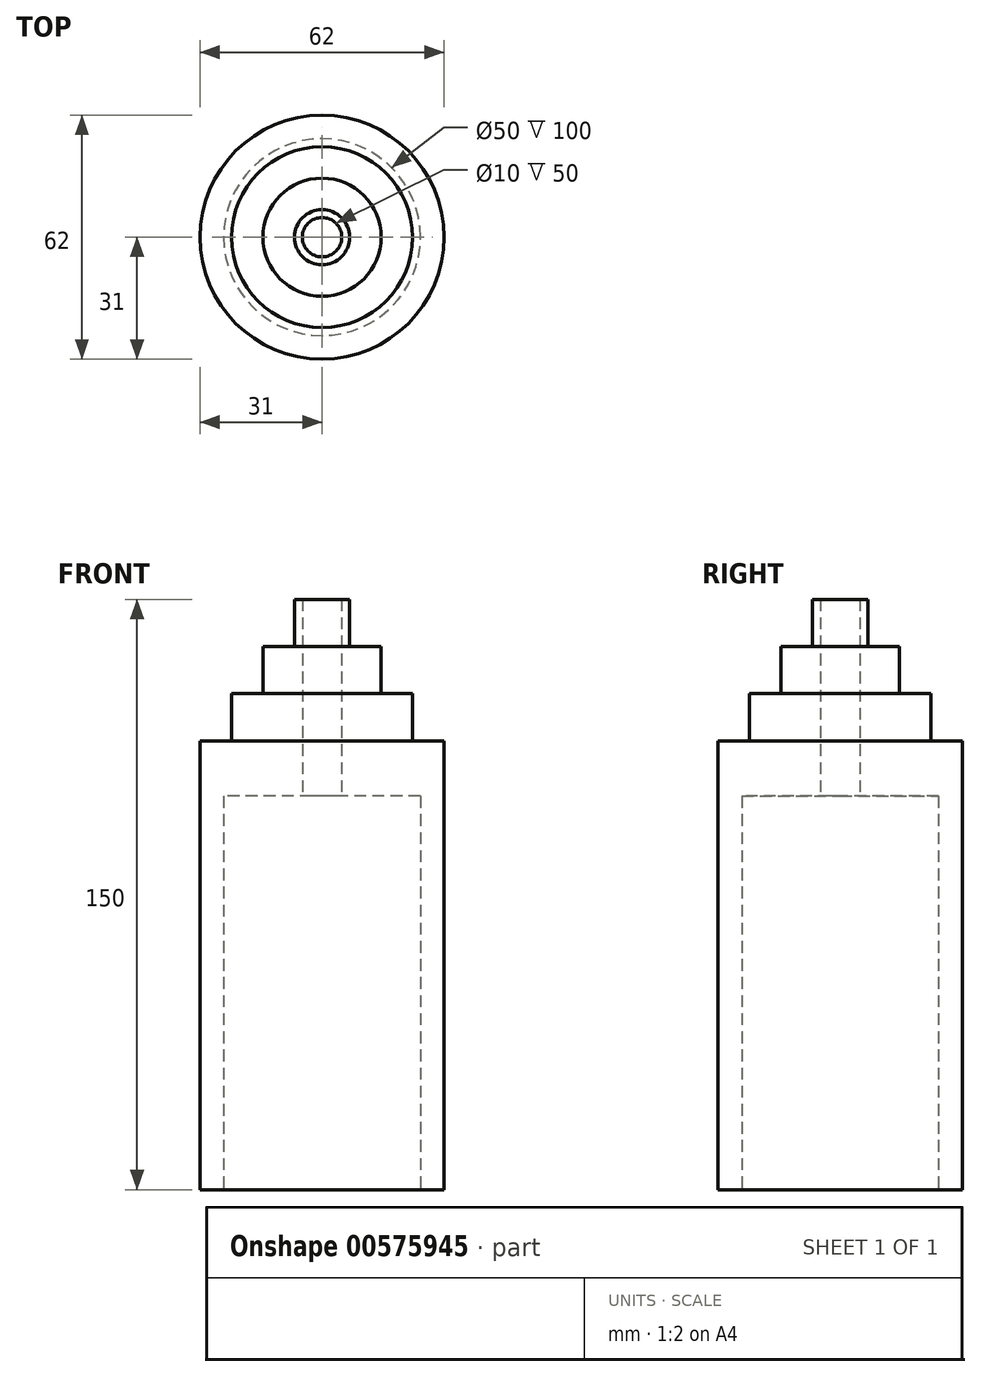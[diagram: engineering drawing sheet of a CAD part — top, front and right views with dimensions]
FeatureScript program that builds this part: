
annotation { "Feature Type Name" : "Feature", "Feature Type Description" : "" }
export const myFeature = defineFeature(function(context is Context, id is Id, definition is map)
    precondition{}
    {
        {
            var Q0;
            Q0=qCreatedBy(makeId("Front.planeOp"),FACE);
            var sketch = newSketch(context, id + "F0", { "sketchPlane" : qUnion([Q0])});
            skLineSegment(sketch, "E0.bottom", {"start": v(0, 0) * mm, "end": v(-31, 0) * mm});
            skLineSegment(sketch, "E0.top", {"start": v(0, 150) * mm, "end": v(-7, 150) * mm});
            skLineSegment(sketch, "E0.left", {"start": v(0, 0) * mm, "end": v(0, 150) * mm});
            skLineSegment(sketch, "E0.right", {"start": v(-31, 0) * mm, "end": v(-31, 114) * mm});
            skPoint(sketch, "E1.visualSharp", {"position": v(-31, 150) * mm});
            skLineSegment(sketch, "E2", {"start": v(-31, 114) * mm, "end": v(-23, 114) * mm});
            skLineSegment(sketch, "E3", {"start": v(-23, 114) * mm, "end": v(-23, 126) * mm});
            skLineSegment(sketch, "E4", {"start": v(-23, 126) * mm, "end": v(-15, 126) * mm});
            skLineSegment(sketch, "E5", {"start": v(-15, 126) * mm, "end": v(-15, 138) * mm});
            skLineSegment(sketch, "E6", {"start": v(-15, 138) * mm, "end": v(-7, 138) * mm});
            skLineSegment(sketch, "E7", {"start": v(-7, 138) * mm, "end": v(-7, 150) * mm});
            skSolve(sketch);
        }
        {
            var Q0;
            Q0=qSketchRegion(id+"F0",true);
            var Q1;
            Q1=sQuery(id+"F0.wireOp",EDGE,"E0.left");
            revolve(context, id + "F1", {"entities" : qUnion([Q0]), "axis" : qUnion([Q1]), "revolveType" : RevolveType.FULL});
        }
        {
            var Q0;
            Q0=qCreatedBy(makeId("Top.planeOp"),FACE);
            var sketch = newSketch(context, id + "F2", { "sketchPlane" : qUnion([Q0])});
            skCircle(sketch, "E8", {"center": v(0, 0) * mm, "radius": 25 * mm});
            skSolve(sketch);
        }
        {
            var Q0;
            Q0=qSketchRegion(id+"F2",true);
            extrude(context, id + "F3", {"entities" : qUnion([Q0]), "operationType" : NewBodyOperationType.REMOVE, "depth" : 100 * mm, "offsetDistance" : 25 * mm});
        }
        {
            var Q0;
            Q0=qCreatedBy(makeId("Top.planeOp"),FACE);
            var sketch = newSketch(context, id + "F4", { "sketchPlane" : qUnion([Q0])});
            skCircle(sketch, "E9", {"center": v(0, 0) * mm, "radius": 5 * mm});
            skSolve(sketch);
        }
        {
            var Q0;
            Q0=qSketchRegion(id+"F4",true);
            extrude(context, id + "F5", {"entities" : qUnion([Q0]), "operationType" : NewBodyOperationType.REMOVE, "endBound" : BoundingType.THROUGH_ALL, "depth" : 25 * mm, "offsetDistance" : 25 * mm});
        }
    });
